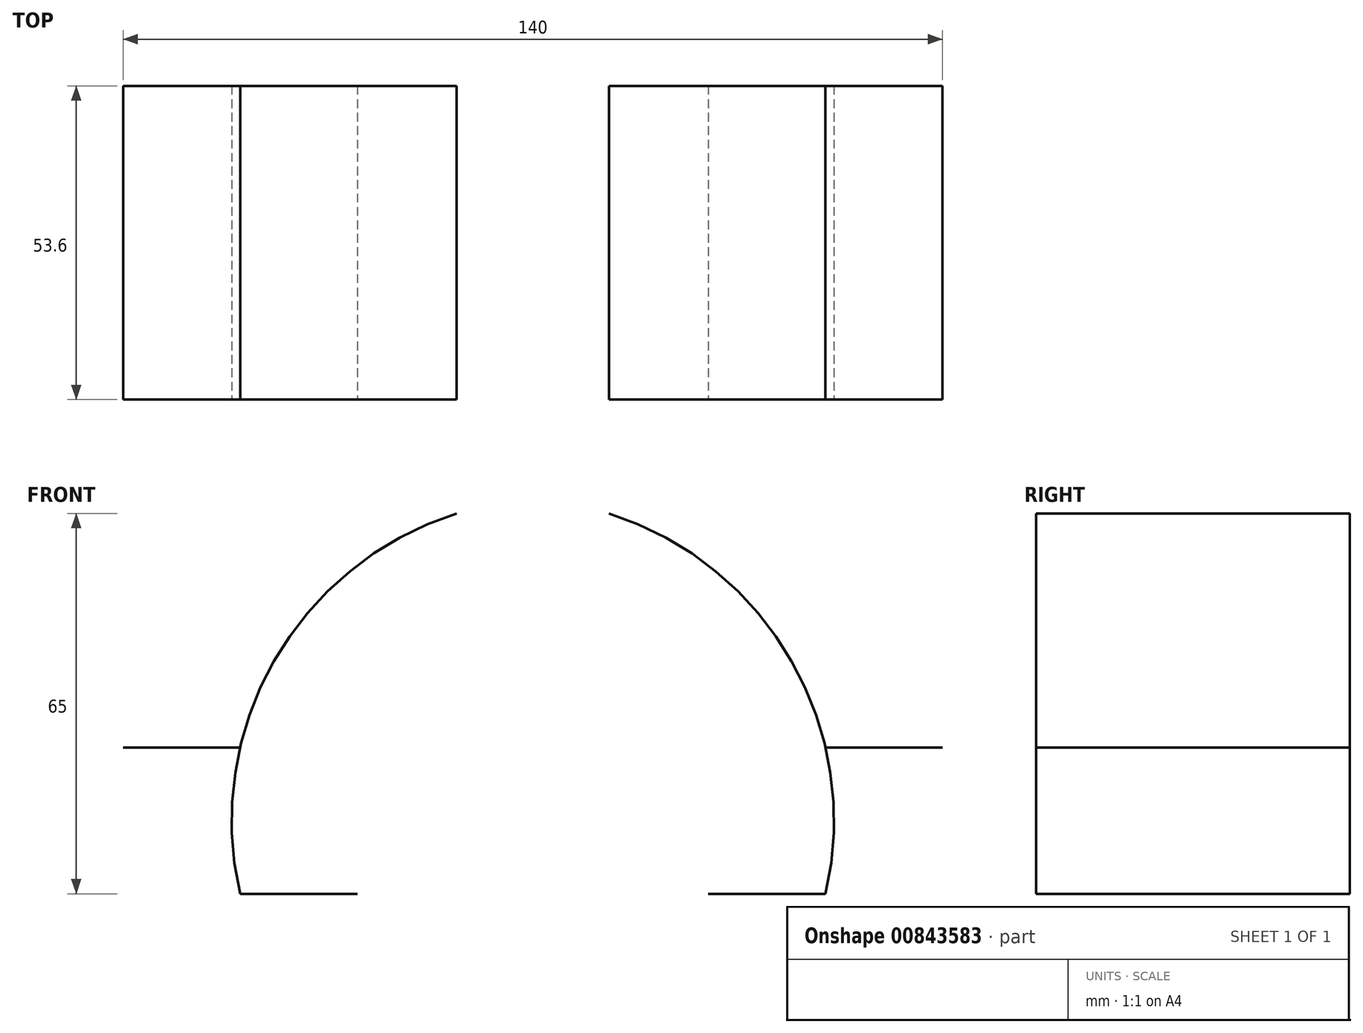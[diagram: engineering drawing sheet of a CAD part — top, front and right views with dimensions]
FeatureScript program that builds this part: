
annotation { "Feature Type Name" : "Feature", "Feature Type Description" : "" }
export const myFeature = defineFeature(function(context is Context, id is Id, definition is map)
    precondition{}
    {
        {
            var Q0;
            Q0=qCreatedBy(makeId("Front.planeOp"),FACE);
            var sketch = newSketch(context, id + "F0", { "sketchPlane" : qUnion([Q0])});
            skLineSegment(sketch, "E0", {"start": v(-70, 0) * mm, "end": v(-50, 0) * mm});
            skLineSegment(sketch, "E1", {"start": v(0, 0) * mm, "end": v(0, 63.17) * mm, "construction": true});
            skLineSegment(sketch, "E2", {"start": v(-13, 40) * mm, "end": v(-13, 39.75) * mm, "construction": true});
            skArc(sketch, "E3", {"start": v(-13, 40) * mm, "mid": v(-36.8, 24.9) * mm, "end": v(-50, 0) * mm});
            skArc(sketch, "E4", {"start": v(-50, 0) * mm, "mid": v(-51.44, -12.5) * mm, "end": v(-50, -25) * mm});
            skLineSegment(sketch, "E5", {"start": v(-50, -25) * mm, "end": v(-30, -25) * mm});
            skArc(sketch, "E6.MirrorCS", {"start": v(13, 40) * mm, "mid": v(36.8, 24.9) * mm, "end": v(50, 0) * mm});
            skLineSegment(sketch, "E7.MirrorCS", {"start": v(70, 0) * mm, "end": v(50, 0) * mm});
            skArc(sketch, "E8.MirrorCS", {"start": v(50, 0) * mm, "mid": v(51.44, -12.5) * mm, "end": v(50, -25) * mm});
            skLineSegment(sketch, "E9.MirrorCS", {"start": v(50, -25) * mm, "end": v(30, -25) * mm});
            skSolve(sketch);
        }
        {
            var Q0;
            Q0 = qSketchRegion(id + "F0", true);
            var Q1;
            Q1=sQuery(id+"F0.wireOp",EDGE,"E3");
            var Q2;
            Q2=sQuery(id+"F0.wireOp",EDGE,"E4");
            var Q3;
            Q3=sQuery(id+"F0.wireOp",EDGE,"E5");
            var Q4;
            Q4=sQuery(id+"F0.wireOp",EDGE,"E6.MirrorCS");
            var Q5;
            Q5=sQuery(id+"F0.wireOp",EDGE,"E8.MirrorCS");
            var Q6;
            Q6=sQuery(id+"F0.wireOp",EDGE,"E9.MirrorCS");
            extrude(context, id + "F1", {"entities" : qUnion([Q0]), "bodyType" : ToolBodyType.SURFACE, "surfaceEntities" : qUnion([Q1, Q2, Q3, Q4, Q5, Q6]), "depth" : 53.6 * mm, "offsetDistance" : 25 * mm});
        }
        {
            var Q0;
            Q0=sQuery(id+"F0.wireOp",EDGE,"E0");
            var Q1;
            Q1=sQuery(id+"F0.wireOp",EDGE,"E7.MirrorCS");
            var Q2;
            Q2=makeQuery(id+"F1.opExtrude","CAP_VERTEX",VERTEX,{"disambiguationData":[OSD([sQuery(id+"F0.wireOp",VERTEX,"E5.start")])],"isStart":false});
            extrude(context, id + "F2", {"bodyType" : ToolBodyType.SURFACE, "surfaceEntities" : qUnion([Q0, Q1]), "endBound" : BoundingType.UP_TO_VERTEX, "depth" : 25 * mm, "endBoundEntityVertex" : qUnion([Q2]), "offsetDistance" : 25 * mm});
        }
    });
